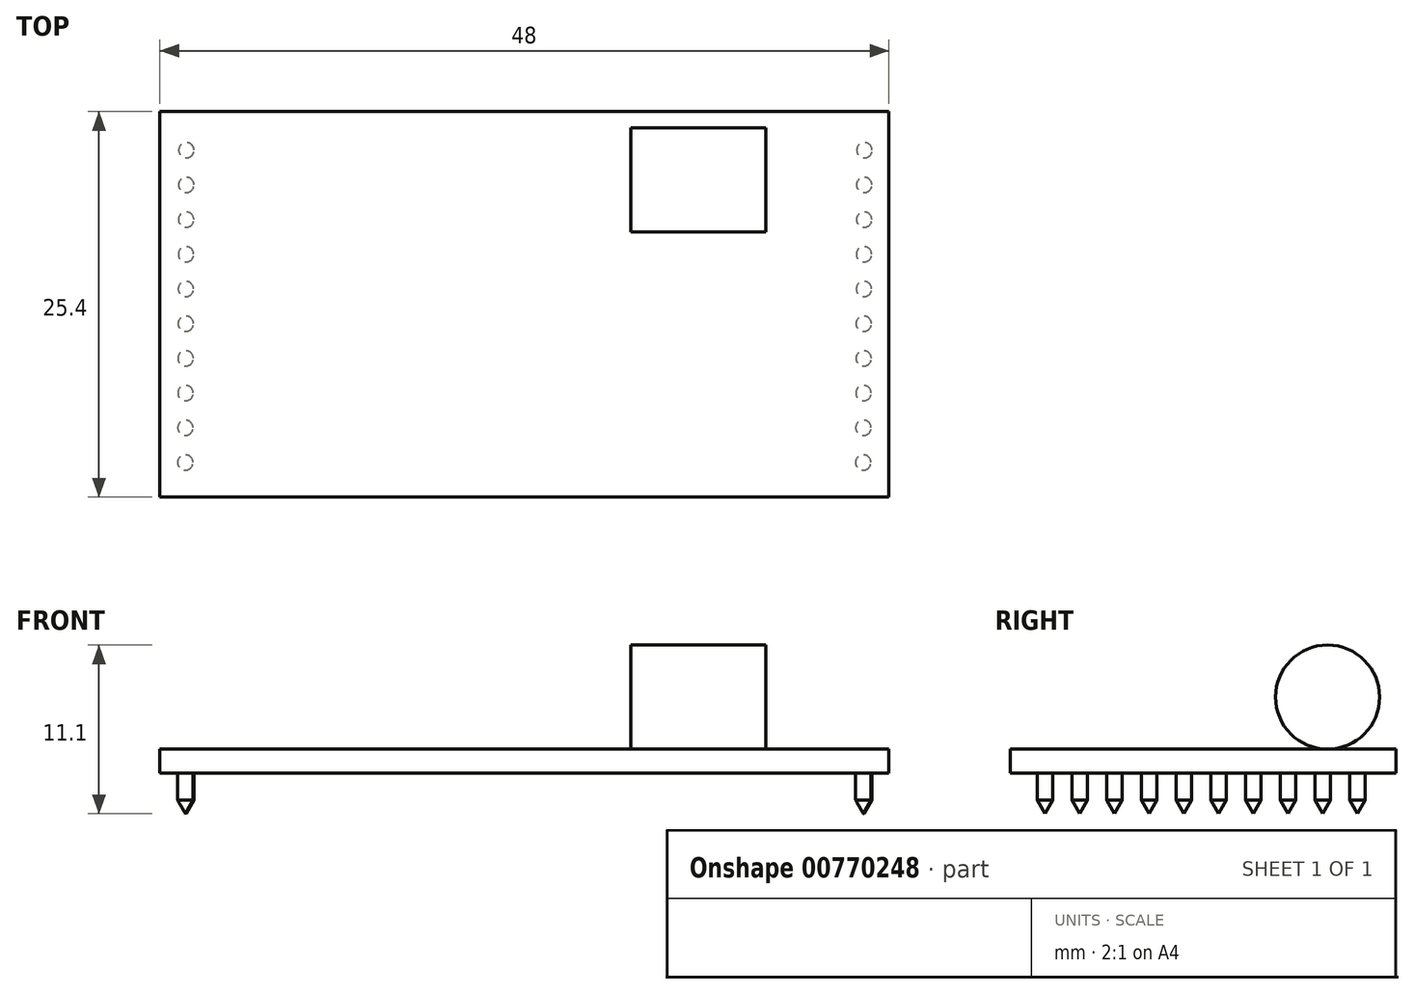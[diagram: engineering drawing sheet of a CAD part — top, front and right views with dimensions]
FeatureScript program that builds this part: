
annotation { "Feature Type Name" : "Feature", "Feature Type Description" : "" }
export const myFeature = defineFeature(function(context is Context, id is Id, definition is map)
    precondition{}
    {
        {
            var Q0;
            Q0=qCreatedBy(makeId("Top.planeOp"),FACE);
            var sketch = newSketch(context, id + "F0", { "sketchPlane" : qUnion([Q0])});
            skLineSegment(sketch, "E0.bottom", {"start": v(-24, -12.7) * mm, "end": v(24, -12.7) * mm});
            skLineSegment(sketch, "E0.top", {"start": v(-24, 12.7) * mm, "end": v(24, 12.7) * mm});
            skLineSegment(sketch, "E0.left", {"start": v(-24, -12.7) * mm, "end": v(-24, 12.7) * mm});
            skLineSegment(sketch, "E0.right", {"start": v(24, -12.7) * mm, "end": v(24, 12.7) * mm});
            skPoint(sketch, "E0.middle", {"position": v(0, 0) * mm});
            skSolve(sketch);
        }
        {
            var Q0;
            Q0=makeQuery(id+"F0.imprint","IMPRINT",FACE,{"disambiguationData":[TD([[makeQuery(id+"F0.imprint","IMPRINT",EDGE,{"derivedFrom":sQuery(id+"F0.wireOp",EDGE,"E0.bottom")}),1.0]])]});
            extrude(context, id + "F1", {"entities" : qUnion([Q0]), "endBound" : BoundingType.SYMMETRIC, "depth" : 1.59 * mm});
        }
        {
            var Q0;
            Q0=makeQuery(id+"F1.opExtrude","CAP_FACE",FACE,{"disambiguationData":[OSD([sQuery(id+"F0.wireOp",EDGE,"E0.bottom"),sQuery(id+"F0.wireOp",EDGE,"E0.top"),sQuery(id+"F0.wireOp",EDGE,"E0.left"),sQuery(id+"F0.wireOp",EDGE,"E0.right")])],"isStart":true});
            var sketch = newSketch(context, id + "F2", { "sketchPlane" : qUnion([Q0])});
            skCircle(sketch, "E1", {"center": v(-22.32, 10.42) * mm, "radius": 0.5 * mm});
            skCircle(sketch, "E2.MirrorC", {"center": v(22.32, 10.42) * mm, "radius": 0.5 * mm});
            skCircle(sketch, "E3.1.0.0", {"center": v(-22.31, 8.14) * mm, "radius": 0.5 * mm});
            skCircle(sketch, "E3.1.0.1", {"center": v(22.33, 8.14) * mm, "radius": 0.5 * mm});
            skCircle(sketch, "E3.2.0.0", {"center": v(-22.3, 5.85) * mm, "radius": 0.5 * mm});
            skCircle(sketch, "E3.2.0.1", {"center": v(22.34, 5.85) * mm, "radius": 0.5 * mm});
            skCircle(sketch, "E3.3.0.0", {"center": v(-22.3, 3.56) * mm, "radius": 0.5 * mm});
            skCircle(sketch, "E3.3.0.1", {"center": v(22.35, 3.56) * mm, "radius": 0.5 * mm});
            skCircle(sketch, "E3.4.0.0", {"center": v(-22.3, 1.28) * mm, "radius": 0.5 * mm});
            skCircle(sketch, "E3.4.0.1", {"center": v(22.35, 1.28) * mm, "radius": 0.5 * mm});
            skCircle(sketch, "E3.5.0.0", {"center": v(-22.28, -1) * mm, "radius": 0.5 * mm});
            skCircle(sketch, "E3.5.0.1", {"center": v(22.36, -1) * mm, "radius": 0.5 * mm});
            skCircle(sketch, "E3.6.0.0", {"center": v(-22.27, -3.3) * mm, "radius": 0.5 * mm});
            skCircle(sketch, "E3.6.0.1", {"center": v(22.37, -3.3) * mm, "radius": 0.5 * mm});
            skCircle(sketch, "E3.7.0.0", {"center": v(-22.27, -5.58) * mm, "radius": 0.5 * mm});
            skCircle(sketch, "E3.7.0.1", {"center": v(22.38, -5.58) * mm, "radius": 0.5 * mm});
            skCircle(sketch, "E3.8.0.0", {"center": v(-22.26, -7.87) * mm, "radius": 0.5 * mm});
            skCircle(sketch, "E3.8.0.1", {"center": v(22.39, -7.87) * mm, "radius": 0.5 * mm});
            skCircle(sketch, "E3.9.0.0", {"center": v(-22.25, -10.15) * mm, "radius": 0.5 * mm});
            skCircle(sketch, "E3.9.0.1", {"center": v(22.4, -10.15) * mm, "radius": 0.5 * mm});
            skLineSegment(sketch, "E3.direction1", {"start": v(-22.32, 10.42) * mm, "end": v(-22.31, 8.14) * mm, "construction": true});
            skSolve(sketch);
        }
        {
            var Q0;
            Q0=qSketchRegion(id+"F2",true);
            extrude(context, id + "F3", {"entities" : qUnion([Q0]), "depth" : 1.78 * mm});
        }
        {
            var Q0;
            Q0=makeQuery(id+"F3.opExtrude","CAP_FACE",FACE,{"disambiguationData":[OSD([sQuery(id+"F2.wireOp",EDGE,"E1")])],"isStart":false});
            var Q1;
            Q1=makeQuery(id+"F3.opExtrude","CAP_FACE",FACE,{"disambiguationData":[OSD([sQuery(id+"F2.wireOp",EDGE,"E3.1.0.0")])],"isStart":false});
            var Q2;
            Q2=makeQuery(id+"F3.opExtrude","CAP_FACE",FACE,{"disambiguationData":[OSD([sQuery(id+"F2.wireOp",EDGE,"E3.2.0.0")])],"isStart":false});
            var Q3;
            Q3=makeQuery(id+"F3.opExtrude","CAP_FACE",FACE,{"disambiguationData":[OSD([sQuery(id+"F2.wireOp",EDGE,"E3.3.0.0")])],"isStart":false});
            var Q4;
            Q4=makeQuery(id+"F3.opExtrude","CAP_FACE",FACE,{"disambiguationData":[OSD([sQuery(id+"F2.wireOp",EDGE,"E3.4.0.0")])],"isStart":false});
            var Q5;
            Q5=makeQuery(id+"F3.opExtrude","CAP_FACE",FACE,{"disambiguationData":[OSD([sQuery(id+"F2.wireOp",EDGE,"E3.5.0.0")])],"isStart":false});
            var Q6;
            Q6=makeQuery(id+"F3.opExtrude","CAP_FACE",FACE,{"disambiguationData":[OSD([sQuery(id+"F2.wireOp",EDGE,"E3.6.0.0")])],"isStart":false});
            var Q7;
            Q7=makeQuery(id+"F3.opExtrude","CAP_FACE",FACE,{"disambiguationData":[OSD([sQuery(id+"F2.wireOp",EDGE,"E3.7.0.0")])],"isStart":false});
            var Q8;
            Q8=makeQuery(id+"F3.opExtrude","CAP_FACE",FACE,{"disambiguationData":[OSD([sQuery(id+"F2.wireOp",EDGE,"E3.8.0.0")])],"isStart":false});
            var Q9;
            Q9=makeQuery(id+"F3.opExtrude","CAP_FACE",FACE,{"disambiguationData":[OSD([sQuery(id+"F2.wireOp",EDGE,"E3.9.0.0")])],"isStart":false});
            var Q10;
            Q10=makeQuery(id+"F3.opExtrude","CAP_FACE",FACE,{"disambiguationData":[OSD([sQuery(id+"F2.wireOp",EDGE,"E2.MirrorC")])],"isStart":false});
            var Q11;
            Q11=makeQuery(id+"F3.opExtrude","CAP_FACE",FACE,{"disambiguationData":[OSD([sQuery(id+"F2.wireOp",EDGE,"E3.1.0.1")])],"isStart":false});
            var Q12;
            Q12=makeQuery(id+"F3.opExtrude","CAP_FACE",FACE,{"disambiguationData":[OSD([sQuery(id+"F2.wireOp",EDGE,"E3.2.0.1")])],"isStart":false});
            var Q13;
            Q13=makeQuery(id+"F3.opExtrude","CAP_FACE",FACE,{"disambiguationData":[OSD([sQuery(id+"F2.wireOp",EDGE,"E3.3.0.1")])],"isStart":false});
            var Q14;
            Q14=makeQuery(id+"F3.opExtrude","CAP_FACE",FACE,{"disambiguationData":[OSD([sQuery(id+"F2.wireOp",EDGE,"E3.4.0.1")])],"isStart":false});
            var Q15;
            Q15=makeQuery(id+"F3.opExtrude","CAP_FACE",FACE,{"disambiguationData":[OSD([sQuery(id+"F2.wireOp",EDGE,"E3.5.0.1")])],"isStart":false});
            var Q16;
            Q16=makeQuery(id+"F3.opExtrude","CAP_FACE",FACE,{"disambiguationData":[OSD([sQuery(id+"F2.wireOp",EDGE,"E3.6.0.1")])],"isStart":false});
            var Q17;
            Q17=makeQuery(id+"F3.opExtrude","CAP_FACE",FACE,{"disambiguationData":[OSD([sQuery(id+"F2.wireOp",EDGE,"E3.7.0.1")])],"isStart":false});
            var Q18;
            Q18=makeQuery(id+"F3.opExtrude","CAP_FACE",FACE,{"disambiguationData":[OSD([sQuery(id+"F2.wireOp",EDGE,"E3.8.0.1")])],"isStart":false});
            var Q19;
            Q19=makeQuery(id+"F3.opExtrude","CAP_FACE",FACE,{"disambiguationData":[OSD([sQuery(id+"F2.wireOp",EDGE,"E3.9.0.1")])],"isStart":false});
            extrude(context, id + "F4", {"entities" : qUnion([Q0, Q1, Q2, Q3, Q4, Q5, Q6, Q7, Q8, Q9, Q10, Q11, Q12, Q13, Q14, Q15, Q16, Q17, Q18, Q19]), "operationType" : NewBodyOperationType.ADD, "depth" : 1.27 * mm, "hasDraft" : true, "draftAngle" : 30 * degree, "draftPullDirection" : true});
        }
        {
            var Q0;
            Q0=makeQuery(id+"F1.opExtrude","CAP_FACE",FACE,{"disambiguationData":[OSD([sQuery(id+"F0.wireOp",EDGE,"E0.bottom"),sQuery(id+"F0.wireOp",EDGE,"E0.top"),sQuery(id+"F0.wireOp",EDGE,"E0.left"),sQuery(id+"F0.wireOp",EDGE,"E0.right")])],"isStart":false});
            var sketch = newSketch(context, id + "F5", { "sketchPlane" : qUnion([Q0])});
            skLineSegment(sketch, "E4.bottom", {"start": v(7, 11.63) * mm, "end": v(15.9, 11.63) * mm});
            skLineSegment(sketch, "E4.top", {"start": v(7, 4.77) * mm, "end": v(15.9, 4.77) * mm});
            skLineSegment(sketch, "E4.left", {"start": v(7, 11.63) * mm, "end": v(7, 4.77) * mm});
            skLineSegment(sketch, "E4.right", {"start": v(15.9, 11.63) * mm, "end": v(15.9, 4.77) * mm});
            skSolve(sketch);
        }
        {
            var Q0;
            Q0=qSketchRegion(id+"F5",true);
            extrude(context, id + "F6", {"entities" : qUnion([Q0]), "depth" : 6.86 * mm});
        }
        {
            var Q0;
            Q0=makeQuery(id+"F6.opExtrude","SWEPT_FACE",FACE,{"disambiguationData":[OSD([sQuery(id+"F5.wireOp",EDGE,"E4.right")])]});
            var sketch = newSketch(context, id + "F7", { "sketchPlane" : qUnion([Q0])});
            skCircle(sketch, "E5", {"center": v(8.2, 4.22) * mm, "radius": 3.43 * mm});
            skPoint(sketch, "E5.centerSnap0", {"position": v(4.77, 4.22) * mm});
            skPoint(sketch, "E5.centerSnap1", {"position": v(8.2, 7.65) * mm});
            skSolve(sketch);
        }
        {
            var Q0;
            {var subQ0=sQuery(id+"F7.wireOp",EDGE,"E5");var subQ1=sQuery(id+"F5.wireOp",EDGE,"E4.right");var subQ2=makeQuery(id+"F6.opExtrude","CAP_EDGE",EDGE,{"disambiguationData":[OSD([subQ1])],"isStart":false});var subQ3=makeQuery(id+"F7.imprint","INTERSECT",VERTEX,{"derivedFrom":[subQ2,subQ0]});Q0=makeQuery(id+"F7.imprint","IMPRINT",FACE,{"disambiguationData":[TD([[makeQuery(id+"F7.imprint","IMPRINT",EDGE,{"disambiguationData":[TD([[subQ3,-1.0]])],"derivedFrom":subQ0}),-1.0]])]});}
            var Q1;
            {var subQ0=sQuery(id+"F7.wireOp",EDGE,"E5");var subQ1=sQuery(id+"F5.wireOp",EDGE,"E4.right");var subQ2=makeQuery(id+"F6.opExtrude","CAP_EDGE",EDGE,{"disambiguationData":[OSD([subQ1])],"isStart":false});var subQ3=makeQuery(id+"F7.imprint","INTERSECT",VERTEX,{"derivedFrom":[subQ2,subQ0]});Q1=makeQuery(id+"F7.imprint","IMPRINT",FACE,{"disambiguationData":[TD([[makeQuery(id+"F7.imprint","IMPRINT",EDGE,{"disambiguationData":[TD([[subQ3,1.0]])],"derivedFrom":subQ0}),-1.0]])]});}
            var Q2;
            {var subQ0=sQuery(id+"F7.wireOp",EDGE,"E5");var subQ1=sQuery(id+"F5.wireOp",EDGE,"E4.right");var subQ4=makeQuery(id+"F6.opExtrude","CAP_EDGE",EDGE,{"disambiguationData":[OSD([subQ1])],"isStart":true});var subQ5=makeQuery(id+"F7.imprint","INTERSECT",VERTEX,{"derivedFrom":[subQ4,subQ0]});Q2=makeQuery(id+"F7.imprint","IMPRINT",FACE,{"disambiguationData":[TD([[makeQuery(id+"F7.imprint","IMPRINT",EDGE,{"disambiguationData":[TD([[subQ5,1.0]])],"derivedFrom":subQ0}),-1.0]])]});}
            var Q3;
            {var subQ0=sQuery(id+"F7.wireOp",EDGE,"E5");var subQ1=sQuery(id+"F5.wireOp",EDGE,"E4.right");var subQ4=makeQuery(id+"F6.opExtrude","CAP_EDGE",EDGE,{"disambiguationData":[OSD([subQ1])],"isStart":true});var subQ5=makeQuery(id+"F7.imprint","INTERSECT",VERTEX,{"derivedFrom":[subQ4,subQ0]});Q3=makeQuery(id+"F7.imprint","IMPRINT",FACE,{"disambiguationData":[TD([[makeQuery(id+"F7.imprint","IMPRINT",EDGE,{"disambiguationData":[TD([[subQ5,-1.0]])],"derivedFrom":subQ0}),-1.0]])]});}
            extrude(context, id + "F8", {"entities" : qUnion([Q0, Q1, Q2, Q3]), "operationType" : NewBodyOperationType.REMOVE, "endBound" : BoundingType.THROUGH_ALL, "oppositeDirection" : true, "depth" : 11.43 * mm});
        }
    });
